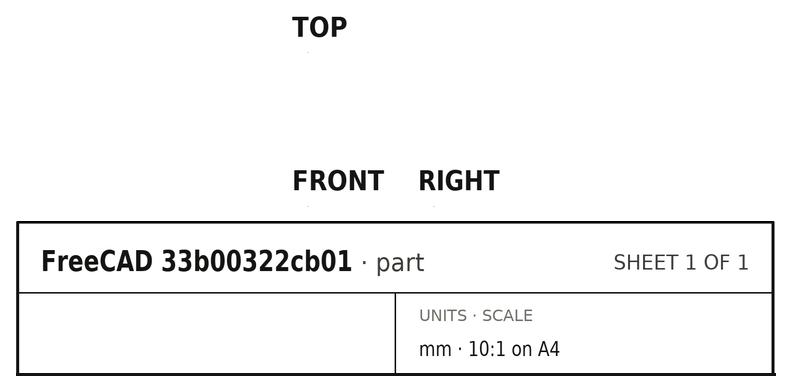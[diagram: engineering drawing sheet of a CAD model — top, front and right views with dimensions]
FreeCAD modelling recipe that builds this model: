
FCSTD DOCUMENT  (FreeCAD 0.21R33694 (Git))
Label: diffPair
License: All rights reserved
LicenseURL: http://en.wikipedia.org/wiki/All_rights_reserved
objects: Part::Part2DObjectPython×22, App::FeaturePython×12, Part::Extrusion×4, Part::Cut×2, Part::FeaturePython×2
note: 30 computed .brp shape members not serialized (recipe doc carries the construction recipe); baked Part::Feature solids carry a one-line shape summary decoded from their .brp

FEATURE [Part::Part2DObjectPython] Wire  # Draft 2D object (typed FeaturePython)
  Area = 0.0014181
  ChamferSize = 0
  Closed = true
  End = (-0.05,0,0)
  FilletRadius = 0
  Length = 0.221006
  MakeFace = true
  Placement = pos=(-0.15,0,0) rot=(0,0,1;0rad)
  Points = (4) [(0,0,0),(0.00545955,0.015,0),(0.0945402,0.015,0),(0.1,-6.12323e-18,0)]
  Start = (-0.15,0,0)
  Subdivisions = 0
FEATURE [Part::Part2DObjectPython] Wire001  # Draft 2D object (typed FeaturePython)
  Area = 0.0014181
  ChamferSize = 0
  Closed = true
  End = (0.15,0,0)
  FilletRadius = 0
  Length = 0.221006
  MakeFace = true
  Placement = pos=(0.05,0,0) rot=(0,0,1;0rad)
  Points = (4) [(0,0,0),(0.00545955,0.015,0),(0.0945402,0.015,0),(0.1,-6.12323e-18,0)]
  Start = (0.05,0,0)
  Subdivisions = 0
FEATURE [Part::Part2DObjectPython] Rectangle  # Draft 2D object (typed FeaturePython)
  Area = 0.13
  ChamferSize = 0
  Columns = 1
  FilletRadius = 0
  Height = 0.1
  Length = 1.3
  MakeFace = true
  Placement = pos=(-0.65,-0.1,0) rot=(0,0,1;0rad)
  Rows = 1
FEATURE [Part::Part2DObjectPython] Rectangle001  # Draft 2D object (typed FeaturePython)
  Area = 0.13
  ChamferSize = 0
  Columns = 1
  FilletRadius = 0
  Height = 0.1
  Length = 1.3
  MakeFace = true
  Placement = pos=(-0.65,0,0) rot=(0,0,1;0rad)
  Rows = 1
FEATURE [Part::Part2DObjectPython] Clone2D  label="Wire (2D)"  # Draft 2D object (typed FeaturePython)
  Fuse = false
  Objects = -> [Wire]
  Placement = pos=(-0.15,0,0) rot=(0,0,1;0rad)
  Scale = (1,1,1)
FEATURE [Part::Part2DObjectPython] Clone2D001  label="Wire001 (2D)"  # Draft 2D object (typed FeaturePython)
  Fuse = false
  Objects = -> [Wire001]
  Placement = pos=(0.05,0,0) rot=(0,0,1;0rad)
  Scale = (1,1,1)
FEATURE [Part::Part2DObjectPython] Clone2D002  label="Rectangle (2D)"  # Draft 2D object (typed FeaturePython)
  Fuse = false
  Objects = -> [Rectangle]
  Placement = pos=(-0.65,-0.1,0) rot=(0,0,1;0rad)
  Scale = (1,1,1)
FEATURE [Part::Part2DObjectPython] Clone2D003  label="Rectangle001 (2D)"  # Draft 2D object (typed FeaturePython)
  Fuse = false
  Objects = -> [Rectangle001]
  Placement = pos=(-0.65,0,0) rot=(0,0,1;0rad)
  Scale = (1,1,1)
FEATURE [Part::Part2DObjectPython] Clone2D004  label="Wire (2D)001"  # Draft 2D object (typed FeaturePython)
  Fuse = false
  Objects = -> [Wire]
  Placement = pos=(-0.15,0,0) rot=(0,0,1;0rad)
  Scale = (1,1,1)
FEATURE [Part::Part2DObjectPython] Clone2D005  label="Wire001 (2D)001"  # Draft 2D object (typed FeaturePython)
  Fuse = false
  Objects = -> [Wire001]
  Placement = pos=(0.05,0,0) rot=(0,0,1;0rad)
  Scale = (1,1,1)
FEATURE [Part::Part2DObjectPython] Clone2D006  label="Rectangle (2D)001"  # Draft 2D object (typed FeaturePython)
  Fuse = false
  Objects = -> [Rectangle]
  Placement = pos=(-0.65,-0.1,0) rot=(0,0,1;0rad)
  Scale = (1,1,1)
FEATURE [Part::Part2DObjectPython] Clone2D007  label="Rectangle001 (2D)001"  # Draft 2D object (typed FeaturePython)
  Fuse = false
  Objects = -> [Rectangle001]
  Placement = pos=(-0.65,0,0) rot=(0,0,1;0rad)
  Scale = (1,1,1)
FEATURE [Part::Extrusion] Extrude004
  Base = -> Clone2D
  Dir = (0,0,1)
  DirMode = 2
  FaceMakerClass = Part::FaceMakerBullseye
  LengthFwd = 2
  LengthRev = 0
  Solid = false
  Symmetric = false
FEATURE [Part::Extrusion] Extrude005
  Base = -> Clone2D001
  Dir = (0,0,1)
  DirMode = 2
  FaceMakerClass = Part::FaceMakerBullseye
  LengthFwd = 2
  LengthRev = 0
  Solid = false
  Symmetric = false
FEATURE [Part::Extrusion] Extrude006
  Base = -> Clone2D002
  Dir = (0,0,1)
  DirMode = 2
  FaceMakerClass = Part::FaceMakerBullseye
  LengthFwd = 2
  LengthRev = 0
  Solid = false
  Symmetric = false
FEATURE [Part::Extrusion] Extrude007
  Base = -> Clone2D003
  Dir = (0,0,1)
  DirMode = 2
  FaceMakerClass = Part::FaceMakerBullseye
  LengthFwd = 2
  LengthRev = 0
  Solid = false
  Symmetric = false
FEATURE [Part::Cut] Cut002
  Base = -> Extrude007
  Tool = -> Extrude004
FEATURE [Part::Cut] Cut003
  Base = -> Cut002
  Tool = -> Extrude005
FEATURE [App::FeaturePython] Text010  label="_Sin(PV){port1}"  # WARN: FeaturePython — macro-defined, semantics opaque (R4)
  Placement = pos=(5.00075,-5.09743,10) rot=(0,0,1;0rad)
  Text = .
FEATURE [App::FeaturePython] Text011  label="_Sout(PV){port2}"  # WARN: FeaturePython — macro-defined, semantics opaque (R4)
  Placement = pos=(5.00075,-5.09743,10) rot=(0,0,1;0rad)
  Text = .
FEATURE [App::FeaturePython] Text012  label="_Lin(1,voltage,in1){v11}"  # WARN: FeaturePython — macro-defined, semantics opaque (R4)
  Placement = pos=(5.00075,-5.09743,10) rot=(0,0,1;0rad)
  Text = .
FEATURE [App::FeaturePython] Text013  label="_Lin(1,current,in1){i11}"  # WARN: FeaturePython — macro-defined, semantics opaque (R4)
  Placement = pos=(5.00075,-5.09743,10) rot=(0,0,1;0rad)
  Text = .
FEATURE [App::FeaturePython] Text014  label="_Lin(2,voltage,in2){v12}"  # WARN: FeaturePython — macro-defined, semantics opaque (R4)
  Placement = pos=(5.00075,-5.09743,10) rot=(0,0,1;0rad)
  Text = .
FEATURE [App::FeaturePython] Text015  label="_Lin(2,current,in2){i12}"  # WARN: FeaturePython — macro-defined, semantics opaque (R4)
  Placement = pos=(5.00075,-5.09743,10) rot=(0,0,1;0rad)
  Text = .
FEATURE [App::FeaturePython] Text016  label="_Lout(3,voltage,out3){v21}"  # WARN: FeaturePython — macro-defined, semantics opaque (R4)
  Placement = pos=(5.00075,-5.09743,10) rot=(0,0,1;0rad)
  Text = .
FEATURE [App::FeaturePython] Text017  label="_Lout(3,current,out3){i21}"  # WARN: FeaturePython — macro-defined, semantics opaque (R4)
  Placement = pos=(5.00075,-5.09743,10) rot=(0,0,1;0rad)
  Text = .
FEATURE [App::FeaturePython] Text018  label="_Lout(4,voltage,out4){v22}"  # WARN: FeaturePython — macro-defined, semantics opaque (R4)
  Placement = pos=(5.00075,-5.09743,10) rot=(0,0,1;0rad)
  Text = .
FEATURE [App::FeaturePython] Text019  label="_Lout(4,current,out4){i22}"  # WARN: FeaturePython — macro-defined, semantics opaque (R4)
  Placement = pos=(5.00075,-5.09743,10) rot=(0,0,1;0rad)
  Text = .
FEATURE [Part::Part2DObjectPython] Wire006  label="_Pi22"  # Draft 2D object (typed FeaturePython)
  Area = 1.4181e-09
  ChamferSize = 0
  Closed = true
  End = (5e-05,-0.0999,4.995)
  FilletRadius = 0
  Length = 0.000221006
  MakeFace = true
  Placement = pos=(0.00015,-0.0999,4.995) rot=(0.707107,0.707107,0;3.14159rad)
  Points = (4) [(0,0,0),(1.5e-05,-5.45983e-06,0),(1.5e-05,-9.45404e-05,0),(0,-0.0001,0)]
  Start = (0.00015,-0.0999,4.995)
  Subdivisions = 0
FEATURE [Part::Part2DObjectPython] Wire007  label="_Pi21"  # Draft 2D object (typed FeaturePython)
  Area = 1.4181e-09
  ChamferSize = 0
  Closed = true
  End = (-0.00015,-0.0999,4.995)
  FilletRadius = 0
  Length = 0.000221006
  MakeFace = true
  Placement = pos=(-5e-05,-0.0999,4.995) rot=(0.707107,0.707107,0;3.14159rad)
  Points = (4) [(0,0,0),(1.5e-05,-5.45983e-06,0),(1.5e-05,-9.45404e-05,0),(0,-0.0001,0)]
  Start = (-5e-05,-0.0999,4.995)
  Subdivisions = 0
FEATURE [Part::Part2DObjectPython] Wire008  label="_Pi11"  # Draft 2D object (typed FeaturePython)
  Area = 1.4181e-09
  ChamferSize = 0
  Closed = true
  End = (-5e-05,-0.0999,4.997)
  FilletRadius = 0
  Length = 0.000221006
  MakeFace = true
  Placement = pos=(-0.00015,-0.0999,4.997) rot=(0,0,1;0rad)
  Points = (4) [(0,0,0),(5.45955e-06,1.5e-05,0),(9.45402e-05,1.5e-05,0),(0.0001,0,0)]
  Start = (-0.00015,-0.0999,4.997)
  Subdivisions = 0
FEATURE [Part::Part2DObjectPython] Wire009  label="_Pi12"  # Draft 2D object (typed FeaturePython)
  Area = 1.4181e-09
  ChamferSize = 0
  Closed = true
  End = (0.00015,-0.0999,4.997)
  FilletRadius = 0
  Length = 0.000221006
  MakeFace = true
  Placement = pos=(5e-05,-0.0999,4.997) rot=(0,0,1;0rad)
  Points = (4) [(0,0,0),(5.45955e-06,1.5e-05,0),(9.45402e-05,1.5e-05,0),(0.0001,0,0)]
  Start = (5e-05,-0.0999,4.997)
  Subdivisions = 0
FEATURE [Part::Part2DObjectPython] Rectangle013  label="_Pport1"  # Draft 2D object (typed FeaturePython)
  Area = 2.6e-07
  ChamferSize = 0
  Columns = 1
  FilletRadius = 0
  Height = 0.0002
  Length = 0.0013
  MakeFace = true
  Placement = pos=(-0.00065,-0.1,4.997) rot=(0,0,1;0rad)
  Rows = 1
FEATURE [Part::Part2DObjectPython] Line  label="_Pv11"  # Draft 2D object (typed FeaturePython)
  Area = 0
  ChamferSize = 0
  Closed = false
  End = (-0.0001,-0.0999,4.997)
  FilletRadius = 0
  Length = 0.0001
  MakeFace = true
  Placement = pos=(0,-0.1,4.997) rot=(0,0,1;0rad)
  Points = (2) [(-0.0001,0,0),(-0.0001,0.0001,0)]
  Start = (-0.0001,-0.1,4.997)
  Subdivisions = 0
FEATURE [Part::Part2DObjectPython] Line004  label="_Pv12"  # Draft 2D object (typed FeaturePython)
  Area = 0
  ChamferSize = 0
  Closed = false
  End = (0.0001,-0.0999,4.997)
  FilletRadius = 0
  Length = 0.0001
  MakeFace = true
  Placement = pos=(0,-0.1,4.997) rot=(0,0,1;0rad)
  Points = (2) [(0.0001,0,0),(0.0001,0.0001,0)]
  Start = (0.0001,-0.1,4.997)
  Subdivisions = 0
FEATURE [Part::Part2DObjectPython] Rectangle014  label="_Pport2"  # Draft 2D object (typed FeaturePython)
  Area = 2.6e-07
  ChamferSize = 0
  Columns = 1
  FilletRadius = 0
  Height = 0.0013
  Length = 0.0002
  MakeFace = true
  Placement = pos=(-0.00065,-0.1,4.995) rot=(0.707107,0.707107,0;3.14159rad)
  Rows = 1
FEATURE [Part::Part2DObjectPython] Line005  label="_Pv21"  # Draft 2D object (typed FeaturePython)
  Area = 0
  ChamferSize = 0
  Closed = false
  End = (-0.0001,-0.0999,4.995)
  FilletRadius = 0
  Length = 0.0001
  MakeFace = true
  Placement = pos=(0,-0.1,4.995) rot=(0.707107,0.707107,0;3.14159rad)
  Points = (2) [(1.38778e-17,-0.0001,0),(0.0001,-0.0001,0)]
  Start = (-0.0001,-0.1,4.995)
  Subdivisions = 0
FEATURE [Part::Part2DObjectPython] Line006  label="_Pv22"  # Draft 2D object (typed FeaturePython)
  Area = 0
  ChamferSize = 0
  Closed = false
  End = (0.0001,-0.0999,4.995)
  FilletRadius = 0
  Length = 0.0001
  MakeFace = true
  Placement = pos=(0,-0.1,4.995) rot=(0.707107,0.707107,0;3.14159rad)
  Points = (2) [(1.38778e-17,0.0001,0),(0.0001,0.0001,0)]
  Start = (0.0001,-0.1,4.995)
  Subdivisions = 0
FEATURE [Part::FeaturePython] BooleanFragments  # WARN: FeaturePython — macro-defined, semantics opaque (R4)
  Mode = 0
  Objects = -> [Extrude006,Cut003]
  Tolerance = 0
FEATURE [Part::FeaturePython] Clone  label="scaled"  # Draft clone (typed FeaturePython)
  AttacherType = Attacher::AttachEngine3D
  Fuse = false
  Objects = -> [BooleanFragments]
  Placement = pos=(0,-0.0999,4.995) rot=(0,0,1;0rad)
  Scale = (0.001,0.001,0.001)
FEATURE [App::FeaturePython] Text020  label="_D(1,2)"  # WARN: FeaturePython — macro-defined, semantics opaque (R4)
  Placement = pos=(5.00075,-5.09743,10) rot=(0,0,1;0rad)
  Text = .
FEATURE [App::FeaturePython] Text021  label="_D(3,4)"  # WARN: FeaturePython — macro-defined, semantics opaque (R4)
  Placement = pos=(5.00075,-5.09743,10) rot=(0,0,1;0rad)
  Text = .
